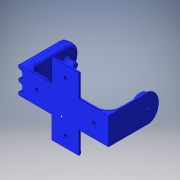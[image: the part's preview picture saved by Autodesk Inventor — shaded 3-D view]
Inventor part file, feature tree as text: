
AUTODESK INVENTOR PART (.ipt)
format: ipt  version: 2016 (Build 200138000, 138)  size: 586,752 bytes
history: native  units: in
note: dims shown in document units (in); Inventor stores cm internally (conversion verified against a paired STEP export)
features: sketch x12, other x3
ambient origin geometry x8: Origin, YZ Plane, XZ Plane, XY Plane, X Axis, Y Axis, Z Axis, Center Point
bodies: Solid1 (feature_tree)
feature tree (15):
  other  "Hip_side.ipt"
  other  "Solid1::Hip_side.ipt"
  other  "TaggingFeature1"
  sketch  "Sketch1"  dims[d0=0.3937in]
  sketch  "Sketch4"
  sketch  "Sketch5"
  sketch  "Sketch7"
  sketch  "Sketch9"
  sketch  "Sketch10"
  sketch  "Sketch15"
  sketch  "Sketch16"
  sketch  "Sketch17"
  sketch  "Sketch18"
  sketch  "Sketch19"
  sketch  "Sketch20"
